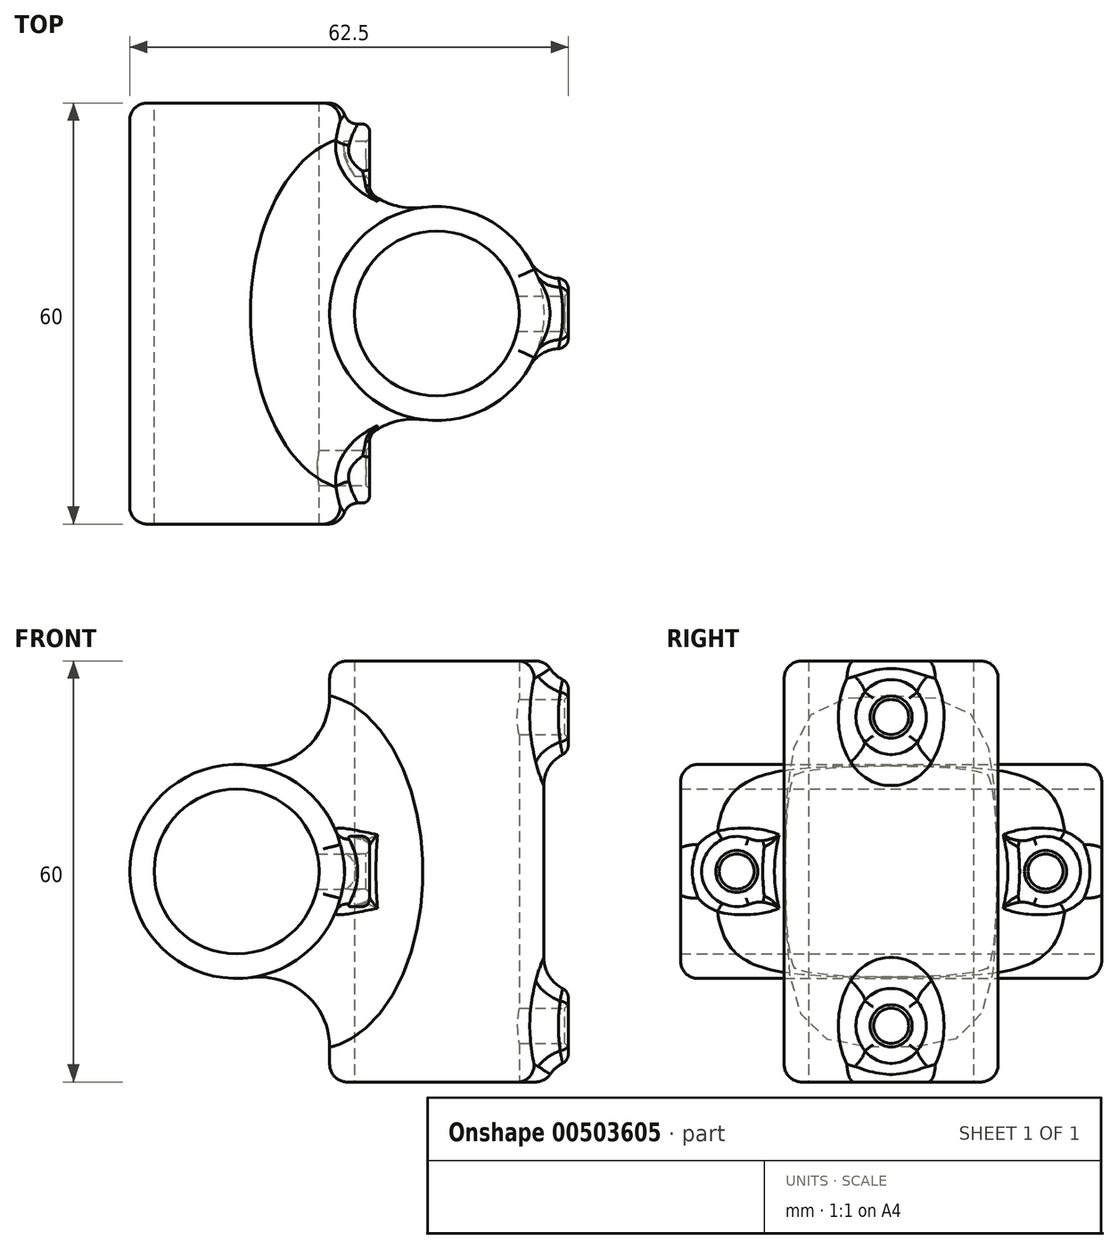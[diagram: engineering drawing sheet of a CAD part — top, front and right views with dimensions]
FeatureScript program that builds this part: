
annotation { "Feature Type Name" : "Feature", "Feature Type Description" : "" }
export const myFeature = defineFeature(function(context is Context, id is Id, definition is map)
    precondition{}
    {
        {
            var Q0;
            Q0=qCreatedBy(makeId("Front.planeOp"),FACE);
            var sketch = newSketch(context, id + "F0", { "sketchPlane" : qUnion([Q0])});
            skCircle(sketch, "E0", {"center": v(-14.25, 0) * mm, "radius": 15.25 * mm});
            skCircle(sketch, "E1", {"center": v(-14.25, 0) * mm, "radius": 11.75 * mm});
            skSolve(sketch);
        }
        {
            var Q0;
            Q0 = qSketchRegion(id + "F0", true);
            extrude(context, id + "F1", {"entities" : qUnion([Q0]), "depth" : 30 * mm, "hasSecondDirection" : true, "secondDirectionOppositeDirection" : true, "secondDirectionDepth" : 30 * mm});
        }
        {
            var Q0;
            Q0=qCreatedBy(makeId("Top.planeOp"),FACE);
            var sketch = newSketch(context, id + "F2", { "sketchPlane" : qUnion([Q0])});
            skCircle(sketch, "E2", {"center": v(14.25, 0) * mm, "radius": 15.25 * mm});
            skCircle(sketch, "E3", {"center": v(14.25, 0) * mm, "radius": 11.75 * mm});
            skSolve(sketch);
        }
        {
            var Q0;
            Q0 = qSketchRegion(id + "F2", true);
            extrude(context, id + "F3", {"entities" : qUnion([Q0]), "operationType" : NewBodyOperationType.ADD, "depth" : 30 * mm, "hasSecondDirection" : true, "secondDirectionOppositeDirection" : true, "secondDirectionDepth" : 30 * mm});
        }
        {
            var Q0;
            Q0=makeQuery(id+"F3.boolean.opBoolean","INTERSECT",EDGE,{"derivedFrom":[makeQuery(id+"F1.opExtrude","SWEPT_FACE",FACE,{"disambiguationData":[OSD([sQuery(id+"F0.wireOp",EDGE,"E0")])]}),makeQuery(id+"F3.opExtrude","SWEPT_FACE",FACE,{"disambiguationData":[OSD([sQuery(id+"F2.wireOp",EDGE,"E2")])]})]});
            fillet(context, id + "F4", {"entities" : qUnion([Q0]), "radius" : 10 * mm, "tangentPropagation" : true, "allowEdgeOverflow" : false});
        }
        {
            var Q0;
            Q0=qCreatedBy(makeId("Right.planeOp"),FACE);
            cPlane(context, id + "F5", {"entities" : qUnion([Q0]), "cplaneType" : CPlaneType.OFFSET, "offset" : 50 * mm, "width" : 150 * mm, "height" : 150 * mm});
        }
        {
            var Q0;
            Q0=qCreatedBy(id+"F5.planeOp",FACE);
            var sketch = newSketch(context, id + "F6", { "sketchPlane" : qUnion([Q0])});
            skCircle(sketch, "E4", {"center": v(0, 22) * mm, "radius": 2.5 * mm});
            skLineSegment(sketch, "E5", {"start": v(0, 0) * mm, "end": v(32.18, 32.18) * mm, "construction": true});
            skCircle(sketch, "E6.MirrorC", {"center": v(0, -22) * mm, "radius": 2.5 * mm});
            skCircle(sketch, "E7.MirrorC", {"center": v(22, 0) * mm, "radius": 2.5 * mm});
            skCircle(sketch, "E8.MirrorC", {"center": v(-22, 0) * mm, "radius": 2.5 * mm});
            skSolve(sketch);
        }
        {
            var Q0;
            Q0=makeQuery(id+"F6.imprint","IMPRINT",FACE,{"disambiguationData":[TD([[makeQuery(id+"F6.imprint","IMPRINT",EDGE,{"derivedFrom":sQuery(id+"F6.wireOp",EDGE,"E7.MirrorC")}),-1.0]])]});
            var Q1;
            Q1=makeQuery(id+"F6.imprint","IMPRINT",FACE,{"disambiguationData":[TD([[makeQuery(id+"F6.imprint","IMPRINT",EDGE,{"derivedFrom":sQuery(id+"F6.wireOp",EDGE,"E8.MirrorC")}),1.0]])]});
            extrude(context, id + "F7", {"entities" : qUnion([Q0, Q1]), "operationType" : NewBodyOperationType.REMOVE, "oppositeDirection" : true, "depth" : 53.5 * mm, "hasSecondDirection" : true, "secondDirectionOppositeDirection" : true, "secondDirectionDepth" : 5 * mm, "offsetDistance" : 25 * mm});
        }
        {
            var Q0;
            Q0=qCreatedBy(makeId("Right.planeOp"),FACE);
            var sketch = newSketch(context, id + "F8", { "sketchPlane" : qUnion([Q0])});
            skCircle(sketch, "E9", {"center": v(-22, 0) * mm, "radius": 2.5 * mm});
            skCircle(sketch, "E10", {"center": v(-22, 0) * mm, "radius": 5 * mm});
            skCircle(sketch, "E11.MirrorC", {"center": v(22, 0) * mm, "radius": 2.5 * mm});
            skCircle(sketch, "E12.MirrorC", {"center": v(22, 0) * mm, "radius": 5 * mm});
            skSolve(sketch);
        }
        {
            var Q0;
            Q0 = qSketchRegion(id + "F8", true);
            extrude(context, id + "F9", {"entities" : qUnion([Q0]), "operationType" : NewBodyOperationType.ADD, "depth" : 4.67 * mm, "offsetDistance" : 25 * mm});
        }
        {
            var Q0;
            Q0=makeQuery(id+"F9.boolean.opBoolean","INTERSECT",EDGE,{"derivedFrom":[makeQuery(id+"F1.opExtrude","SWEPT_FACE",FACE,{"disambiguationData":[OSD([sQuery(id+"F0.wireOp",EDGE,"E0")])]}),makeQuery(id+"F9.opExtrude","SWEPT_FACE",FACE,{"disambiguationData":[OSD([sQuery(id+"F8.wireOp",EDGE,"E10")])]})]});
            var Q1;
            Q1=makeQuery(id+"F9.boolean.opBoolean","INTERSECT",EDGE,{"derivedFrom":[makeQuery(id+"F4.opFillet","BLEND_FACE",FACE,{"disambiguationData":[OSD([sQuery(id+"F0.wireOp",EDGE,"E0"),sQuery(id+"F2.wireOp",EDGE,"E2")])]}),makeQuery(id+"F9.opExtrude","CAP_FACE",FACE,{"disambiguationData":[OSD([sQuery(id+"F8.wireOp",EDGE,"E9"),sQuery(id+"F8.wireOp",EDGE,"E10")])],"isStart":false})]});
            fillet(context, id + "F10", {"entities" : qUnion([Q0, Q1]), "radius" : 2 * mm, "tangentPropagation" : true, "allowEdgeOverflow" : false});
        }
        {
            var Q0;
            Q0=makeQuery(id+"F9.boolean.opBoolean","INTERSECT",EDGE,{"derivedFrom":[makeQuery(id+"F1.opExtrude","SWEPT_FACE",FACE,{"disambiguationData":[OSD([sQuery(id+"F0.wireOp",EDGE,"E0")])]}),makeQuery(id+"F9.opExtrude","SWEPT_FACE",FACE,{"disambiguationData":[OSD([sQuery(id+"F8.wireOp",EDGE,"E12.MirrorC")])]})]});
            var Q1;
            Q1=makeQuery(id+"F9.boolean.opBoolean","INTERSECT",EDGE,{"derivedFrom":[makeQuery(id+"F4.opFillet","BLEND_FACE",FACE,{"disambiguationData":[OSD([sQuery(id+"F0.wireOp",EDGE,"E0"),sQuery(id+"F2.wireOp",EDGE,"E2")])]}),makeQuery(id+"F9.opExtrude","CAP_FACE",FACE,{"disambiguationData":[OSD([sQuery(id+"F8.wireOp",EDGE,"E11.MirrorC"),sQuery(id+"F8.wireOp",EDGE,"E12.MirrorC")])],"isStart":false})]});
            fillet(context, id + "F11", {"entities" : qUnion([Q0, Q1]), "radius" : 2 * mm, "tangentPropagation" : true, "allowEdgeOverflow" : false});
        }
        {
            var Q0;
            Q0=qCreatedBy(id+"F5.planeOp",FACE);
            var sketch = newSketch(context, id + "F12", { "sketchPlane" : qUnion([Q0])});
            skCircle(sketch, "E13", {"center": v(0, 22) * mm, "radius": 2.5 * mm});
            skCircle(sketch, "E14", {"center": v(0, -22) * mm, "radius": 2.5 * mm});
            skLineSegment(sketch, "E15", {"start": v(0, 0) * mm, "end": v(0, 22) * mm, "construction": true});
            skLineSegment(sketch, "E16", {"start": v(0, 0) * mm, "end": v(-22, 0) * mm, "construction": true});
            skLineSegment(sketch, "E17", {"start": v(0, 0) * mm, "end": v(0, -22) * mm, "construction": true});
            skSolve(sketch);
        }
        {
            var Q0;
            Q0 = qSketchRegion(id + "F12", true);
            extrude(context, id + "F13", {"entities" : qUnion([Q0]), "operationType" : NewBodyOperationType.REMOVE, "oppositeDirection" : true, "depth" : 30 * mm, "offsetDistance" : 25 * mm});
        }
        {
            var Q0;
            Q0=qCreatedBy(makeId("Right.planeOp"),FACE);
            cPlane(context, id + "F14", {"entities" : qUnion([Q0]), "cplaneType" : CPlaneType.OFFSET, "offset" : 26.5 * mm, "width" : 150 * mm, "height" : 150 * mm});
        }
        {
            var Q0;
            Q0=qCreatedBy(id+"F14.planeOp",FACE);
            var sketch = newSketch(context, id + "F15", { "sketchPlane" : qUnion([Q0])});
            skCircle(sketch, "E18", {"center": v(0, 22) * mm, "radius": 2.5 * mm});
            skCircle(sketch, "E19", {"center": v(0, -22) * mm, "radius": 2.5 * mm});
            skCircle(sketch, "E20", {"center": v(0, 22) * mm, "radius": 5 * mm});
            skCircle(sketch, "E21", {"center": v(0, -22) * mm, "radius": 5 * mm});
            skSolve(sketch);
        }
        {
            var Q0;
            Q0 = qSketchRegion(id + "F15", true);
            extrude(context, id + "F16", {"entities" : qUnion([Q0]), "operationType" : NewBodyOperationType.ADD, "depth" : 6.5 * mm, "offsetDistance" : 25 * mm});
        }
        {
            var Q0;
            Q0=makeQuery(id+"F16.boolean.opBoolean","INTERSECT",EDGE,{"derivedFrom":[makeQuery(id+"F3.opExtrude","SWEPT_FACE",FACE,{"disambiguationData":[OSD([sQuery(id+"F2.wireOp",EDGE,"E2")])]}),makeQuery(id+"F16.opExtrude","SWEPT_FACE",FACE,{"disambiguationData":[OSD([sQuery(id+"F15.wireOp",EDGE,"E20")])]})]});
            var Q1;
            Q1=makeQuery(id+"F16.boolean.opBoolean","INTERSECT",EDGE,{"derivedFrom":[makeQuery(id+"F3.opExtrude","SWEPT_FACE",FACE,{"disambiguationData":[OSD([sQuery(id+"F2.wireOp",EDGE,"E2")])]}),makeQuery(id+"F16.opExtrude","SWEPT_FACE",FACE,{"disambiguationData":[OSD([sQuery(id+"F15.wireOp",EDGE,"E21")])]})]});
            fillet(context, id + "F17", {"entities" : qUnion([Q0, Q1]), "radius" : 5 * mm, "tangentPropagation" : true, "allowEdgeOverflow" : false});
        }
        {
            var Q0;
            {var subQ0=sQuery(id+"F8.wireOp",EDGE,"E10");var subQ1=makeQuery(id+"F4.opFillet","BLEND_FACE",FACE,{"disambiguationData":[OSD([sQuery(id+"F0.wireOp",EDGE,"E0"),sQuery(id+"F2.wireOp",EDGE,"E2")])]});Q0=makeQuery(id+"F10.opFillet","BLEND_EDGE",EDGE,{"blendedFrom":[makeQuery(id+"F9.boolean.opBoolean","INTERSECT",EDGE,{"derivedFrom":[subQ1,makeQuery(id+"F9.opExtrude","CAP_FACE",FACE,{"disambiguationData":[OSD([sQuery(id+"F8.wireOp",EDGE,"E9"),subQ0])],"isStart":false})]}),makeQuery(id+"F9.boolean.opBoolean","INTERSECT",EDGE,{"disambiguationData":[OD(0.0)],"derivedFrom":[subQ1,makeQuery(id+"F9.opExtrude","SWEPT_FACE",FACE,{"disambiguationData":[OSD([subQ0])]})]})],"blendedInto":[]});}
            var Q1;
            {var subQ0=sQuery(id+"F8.wireOp",EDGE,"E10");var subQ1=makeQuery(id+"F4.opFillet","BLEND_FACE",FACE,{"disambiguationData":[OSD([sQuery(id+"F0.wireOp",EDGE,"E0"),sQuery(id+"F2.wireOp",EDGE,"E2")])]});Q1=makeQuery(id+"F10.opFillet","BLEND_EDGE",EDGE,{"blendedFrom":[makeQuery(id+"F9.boolean.opBoolean","INTERSECT",EDGE,{"derivedFrom":[subQ1,makeQuery(id+"F9.opExtrude","CAP_FACE",FACE,{"disambiguationData":[OSD([sQuery(id+"F8.wireOp",EDGE,"E9"),subQ0])],"isStart":false})]}),makeQuery(id+"F9.boolean.opBoolean","INTERSECT",EDGE,{"disambiguationData":[OD(1.0)],"derivedFrom":[subQ1,makeQuery(id+"F9.opExtrude","SWEPT_FACE",FACE,{"disambiguationData":[OSD([subQ0])]})]})],"blendedInto":[]});}
            var Q2;
            {var subQ0=sQuery(id+"F8.wireOp",EDGE,"E12.MirrorC");var subQ1=makeQuery(id+"F4.opFillet","BLEND_FACE",FACE,{"disambiguationData":[OSD([sQuery(id+"F0.wireOp",EDGE,"E0"),sQuery(id+"F2.wireOp",EDGE,"E2")])]});Q2=makeQuery(id+"F11.opFillet","BLEND_EDGE",EDGE,{"blendedFrom":[makeQuery(id+"F9.boolean.opBoolean","INTERSECT",EDGE,{"derivedFrom":[subQ1,makeQuery(id+"F9.opExtrude","CAP_FACE",FACE,{"disambiguationData":[OSD([sQuery(id+"F8.wireOp",EDGE,"E11.MirrorC"),subQ0])],"isStart":false})]}),makeQuery(id+"F9.boolean.opBoolean","INTERSECT",EDGE,{"disambiguationData":[OD(0.0)],"derivedFrom":[subQ1,makeQuery(id+"F9.opExtrude","SWEPT_FACE",FACE,{"disambiguationData":[OSD([subQ0])]})]})],"blendedInto":[]});}
            var Q3;
            {var subQ0=sQuery(id+"F8.wireOp",EDGE,"E12.MirrorC");var subQ1=makeQuery(id+"F4.opFillet","BLEND_FACE",FACE,{"disambiguationData":[OSD([sQuery(id+"F0.wireOp",EDGE,"E0"),sQuery(id+"F2.wireOp",EDGE,"E2")])]});Q3=makeQuery(id+"F11.opFillet","BLEND_EDGE",EDGE,{"blendedFrom":[makeQuery(id+"F9.boolean.opBoolean","INTERSECT",EDGE,{"derivedFrom":[subQ1,makeQuery(id+"F9.opExtrude","CAP_FACE",FACE,{"disambiguationData":[OSD([sQuery(id+"F8.wireOp",EDGE,"E11.MirrorC"),subQ0])],"isStart":false})]}),makeQuery(id+"F9.boolean.opBoolean","INTERSECT",EDGE,{"disambiguationData":[OD(1.0)],"derivedFrom":[subQ1,makeQuery(id+"F9.opExtrude","SWEPT_FACE",FACE,{"disambiguationData":[OSD([subQ0])]})]})],"blendedInto":[]});}
            fillet(context, id + "F18", {"entities" : qUnion([Q0, Q1, Q2, Q3]), "radius" : 1 * mm, "tangentPropagation" : true, "allowEdgeOverflow" : false});
        }
        {
            var Q0;
            {var subQ0=sQuery(id+"F15.wireOp",EDGE,"E20");Q0=makeQuery(id+"F17.opFillet","BLEND_EDGE",EDGE,{"disambiguationData":[OD(0.0)],"blendedFrom":[makeQuery(id+"F16.boolean.opBoolean","INTERSECT",EDGE,{"derivedFrom":[makeQuery(id+"F3.opExtrude","SWEPT_FACE",FACE,{"disambiguationData":[OSD([sQuery(id+"F2.wireOp",EDGE,"E2")])]}),makeQuery(id+"F16.opExtrude","SWEPT_FACE",FACE,{"disambiguationData":[OSD([subQ0])]})]}),makeQuery(id+"F16.opExtrude","CAP_FACE",FACE,{"disambiguationData":[OSD([sQuery(id+"F15.wireOp",EDGE,"E18"),subQ0])],"isStart":false})],"blendedInto":[makeQuery(id+"F16.opExtrude","CAP_FACE",FACE,{"disambiguationData":[OSD([sQuery(id+"F15.wireOp",EDGE,"E18"),subQ0])],"isStart":false})]});}
            var Q1;
            {var subQ0=sQuery(id+"F15.wireOp",EDGE,"E21");Q1=makeQuery(id+"F17.opFillet","BLEND_EDGE",EDGE,{"disambiguationData":[OD(1.0)],"blendedFrom":[makeQuery(id+"F16.boolean.opBoolean","INTERSECT",EDGE,{"derivedFrom":[makeQuery(id+"F3.opExtrude","SWEPT_FACE",FACE,{"disambiguationData":[OSD([sQuery(id+"F2.wireOp",EDGE,"E2")])]}),makeQuery(id+"F16.opExtrude","SWEPT_FACE",FACE,{"disambiguationData":[OSD([subQ0])]})]}),makeQuery(id+"F16.opExtrude","CAP_FACE",FACE,{"disambiguationData":[OSD([sQuery(id+"F15.wireOp",EDGE,"E19"),subQ0])],"isStart":false})],"blendedInto":[makeQuery(id+"F16.opExtrude","CAP_FACE",FACE,{"disambiguationData":[OSD([sQuery(id+"F15.wireOp",EDGE,"E19"),subQ0])],"isStart":false})]});}
            fillet(context, id + "F19", {"entities" : qUnion([Q0, Q1]), "radius" : 1.5 * mm, "tangentPropagation" : true, "allowEdgeOverflow" : false});
        }
        {
            var Q0;
            Q0=makeQuery(id+"F9.opExtrude","CAP_EDGE",EDGE,{"disambiguationData":[OSD([sQuery(id+"F8.wireOp",EDGE,"E9")])],"isStart":false});
            var Q1;
            Q1=makeQuery(id+"F16.opExtrude","CAP_EDGE",EDGE,{"disambiguationData":[OSD([sQuery(id+"F15.wireOp",EDGE,"E18")])],"isStart":false});
            var Q2;
            Q2=makeQuery(id+"F16.opExtrude","CAP_EDGE",EDGE,{"disambiguationData":[OSD([sQuery(id+"F15.wireOp",EDGE,"E19")])],"isStart":false});
            var Q3;
            Q3=makeQuery(id+"F9.opExtrude","CAP_EDGE",EDGE,{"disambiguationData":[OSD([sQuery(id+"F8.wireOp",EDGE,"E11.MirrorC")])],"isStart":false});
            chamfer(context, id + "F20", {"entities" : qUnion([Q0, Q1, Q2, Q3]), "width" : 0.5 * mm, "tangentPropagation" : true});
        }
        {
            var Q0;
            Q0=makeQuery(id+"F3.opExtrude","CAP_EDGE",EDGE,{"disambiguationData":[OSD([sQuery(id+"F2.wireOp",EDGE,"E2")])],"isStart":false});
            var Q1;
            Q1=makeQuery(id+"F3.opExtrude","CAP_EDGE",EDGE,{"disambiguationData":[OSD([sQuery(id+"F2.wireOp",EDGE,"E2")])],"isStart":true});
            var Q2;
            Q2=makeQuery(id+"F1.opExtrude","CAP_EDGE",EDGE,{"disambiguationData":[OSD([sQuery(id+"F0.wireOp",EDGE,"E0")])],"isStart":true});
            var Q3;
            Q3=makeQuery(id+"F1.opExtrude","CAP_EDGE",EDGE,{"disambiguationData":[OSD([sQuery(id+"F0.wireOp",EDGE,"E0")])],"isStart":false});
            fillet(context, id + "F21", {"entities" : qUnion([Q0, Q1, Q2, Q3]), "radius" : 2.5 * mm, "tangentPropagation" : true, "allowEdgeOverflow" : false});
        }
    });
